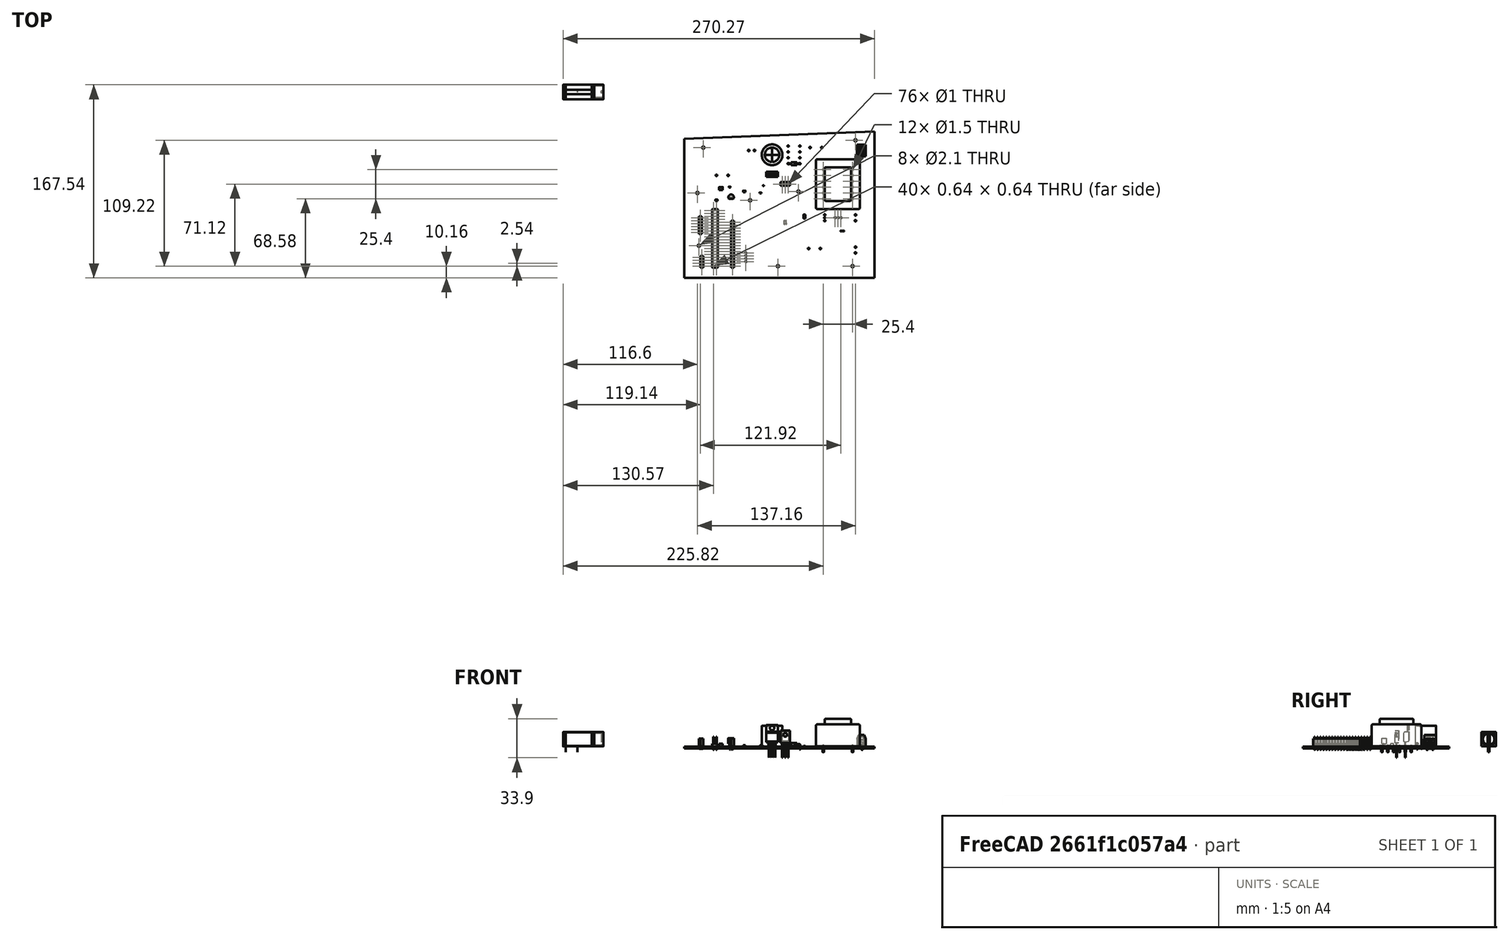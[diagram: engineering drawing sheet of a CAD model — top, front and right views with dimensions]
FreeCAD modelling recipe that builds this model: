
FCSTD DOCUMENT  (FreeCAD 0.19R24267 (Git))
Label: pcb_cad
License: All rights reserved
LicenseURL: http://en.wikipedia.org/wiki/All_rights_reserved
objects: App::Link×29, Part::Feature×23, App::Part×5, PartDesign::CoordinateSystem×1, Sketcher::SketchObject×1, Part::Compound2×1
note: 25 computed .brp shape members not serialized (recipe doc carries the construction recipe); baked Part::Feature solids carry a one-line shape summary decoded from their .brp

FEATURE [PartDesign::CoordinateSystem] Local_CS_53f5
  AttacherType = Attacher::AttachEngine3D
FEATURE [Part::Feature] Pcb_53f5
  shape: bbox 165.1 x 127 x 1.6 mm, 138 faces (baked)
FEATURE [Sketcher::SketchObject] PCB_Sketch_53f5
  FullyConstrained = false
  sketch-geometry (4):
    g0: LineSegment StartX=267.97 StartY=-34.29 StartZ=0 EndX=102.87 EndY=-40.64 EndZ=0
    g1: LineSegment StartX=267.97 StartY=-161.29 StartZ=0 EndX=267.97 EndY=-34.29 EndZ=0
    g2: LineSegment StartX=102.87 StartY=-161.29 StartZ=0 EndX=267.97 EndY=-161.29 EndZ=0
    g3: LineSegment StartX=102.87 StartY=-40.64 StartZ=0 EndX=102.87 EndY=-161.29 EndZ=0
  constraints (4):
    c: Coincident(g2,g3)
    c: Coincident(g0,g3)
    c: Coincident(g1,g2)
    c: Coincident(g0,g1)
FEATURE [App::Part] Board_Geoms_53f5
  Group = -> [Local_CS_53f5,Pcb_53f5,PCB_Sketch_53f5]
  Origin = -> Origin
FEATURE [Part::Feature] Shape  label="P1_User Library-Terminal-Screw-3A-2way_606F4117"
  Placement = pos=(256.54,-50.8,0) rot=(0.57735,0.57735,0.57735;2.0944rad)
  shape: bbox 7.6 x 10.6 x 13 mm, 121 faces (baked)
FEATURE [App::Link] P1_User_Library_Terminal_Screw_3A_2way_606F4117_ln_  label="J8_User Library-Terminal-Screw-3A-2way_606F4101"
  LinkPlacement = pos=(251.46,-137.16,0) rot=(0.57735,0.57735,0.57735;2.0944rad)
  LinkedObject = -> Shape
  Placement = pos=(251.46,-137.16,0) rot=(0.57735,0.57735,0.57735;2.0944rad)
FEATURE [App::Link] P1_User_Library_Terminal_Screw_3A_2way_606F4117_ln_001  label="J2_User Library-Terminal-Screw-3A-2way_606DFC80"
  LinkPlacement = pos=(161.29,-50.8,0) rot=(0,0.707107,0.707107;3.14159rad)
  LinkedObject = -> Shape
  Placement = pos=(161.29,-50.8,0) rot=(0,0.707107,0.707107;3.14159rad)
FEATURE [Part::Feature] Shape001  label="J1_PinHeader_2x20_P254mm_Vertical_606DFC5E"
  Placement = pos=(128.27,-102.87,0) rot=(0,0,1;0rad)
  shape: bbox 5.08 x 50.8 x 11.54 mm, 844 faces (baked)
FEATURE [Part::Feature] Shape002  label="R1_R_1206_3216Metric_606F4180"
  Placement = pos=(207.01,-108.142,0) rot=(0,0,-1;1.5708rad)
  shape: bbox 1.6 x 3.2 x 0.55 mm, 26 faces (baked)
FEATURE [Part::Feature] Shape003  label="D11_D_1206_606F3DCA"
  Placement = pos=(190.5,-113.16,-1.6) rot=(0.707107,0.707107,0;3.14159rad)
  shape: bbox 1.87 x 3.4 x 0.96 mm, 39 faces (baked)
FEATURE [Part::Feature] Shape004  label="U2_TO-220-3_Vertical_606F427F"
  Placement = pos=(176.53,-72.39,0) rot=(0,0,1;0rad)
  shape: bbox 10.25 x 4.455 x 28.53 mm, 48 faces (baked)
FEATURE [App::Link] U2_TO_220_3_Vertical_606F427F_ln_  label="U1_TO-220-3_Vertical_606F4265"
  LinkPlacement = pos=(224.79,-106.68,0) rot=(0,0,-1;1.5708rad)
  LinkedObject = -> Shape004
  Placement = pos=(224.79,-106.68,0) rot=(0,0,-1;1.5708rad)
FEATURE [Part::Feature] Shape005  label="T1_Transformer_37x046_606F424B"
  Placement = pos=(248.92,-72.39,0) rot=(0,0,-1;1.5708rad)
  shape: bbox 38.1 x 43.18 x 29.15 mm, 83 faces, 13 solids (baked)
FEATURE [App::Link] R1_R_1206_3216Metric_606F4180_ln_  label="R11_R_1206_3216Metric_606F422A"
  LinkPlacement = pos=(151.13,-82.55,0) rot=(0,0,1;0rad)
  LinkedObject = -> Shape002
  Placement = pos=(151.13,-82.55,0) rot=(0,0,1;0rad)
FEATURE [App::Link] R1_R_1206_3216Metric_606F4180_ln_001  label="R10_R_1206_3216Metric_606F4219"
  LinkPlacement = pos=(190.5,-106.873,-1.6) rot=(0.707107,0.707107,0;3.14159rad)
  LinkedObject = -> Shape002
  Placement = pos=(190.5,-106.873,-1.6) rot=(0.707107,0.707107,0;3.14159rad)
FEATURE [App::Link] R1_R_1206_3216Metric_606F4180_ln_002  label="R9_R_1206_3216Metric_606F4208"
  LinkPlacement = pos=(187.96,-66.04,0) rot=(0,0,1;3.14159rad)
  LinkedObject = -> Shape002
  Placement = pos=(187.96,-66.04,0) rot=(0,0,1;3.14159rad)
FEATURE [App::Link] R1_R_1206_3216Metric_606F4180_ln_003  label="R8_R_1206_3216Metric_606F41F7"
  LinkPlacement = pos=(177.8,-83.82,0) rot=(0,0,1;0rad)
  LinkedObject = -> Shape002
  Placement = pos=(177.8,-83.82,0) rot=(0,0,1;0rad)
FEATURE [App::Link] R1_R_1206_3216Metric_606F4180_ln_004  label="R7_R_1206_3216Metric_606F41E6"
  LinkPlacement = pos=(216.94,-105.984,-1.6) rot=(-0.707107,0.707107,0;3.14159rad)
  LinkedObject = -> Shape002
  Placement = pos=(216.94,-105.984,-1.6) rot=(-0.707107,0.707107,0;3.14159rad)
FEATURE [Part::Feature] Shape006  label="R6_R_0402_1005Metric_606F41D5"
  Placement = pos=(171.45,-81.28,0) rot=(0,0,1;3.14159rad)
  shape: bbox 1 x 0.5 x 0.35 mm, 26 faces (baked)
FEATURE [App::Link] R6_R_0402_1005Metric_606F41D5_ln_  label="R5_R_0402_1005Metric_606F41C4"
  LinkPlacement = pos=(212.09,-118.87,0) rot=(0,0,-1;1.5708rad)
  LinkedObject = -> Shape006
  Placement = pos=(212.09,-118.87,0) rot=(0,0,-1;1.5708rad)
FEATURE [App::Link] R1_R_1206_3216Metric_606F4180_ln_005  label="R4_R_1206_3216Metric_606F41B3"
  LinkPlacement = pos=(168.91,-77.47,0) rot=(0,0,1;3.14159rad)
  LinkedObject = -> Shape002
  Placement = pos=(168.91,-77.47,0) rot=(0,0,1;3.14159rad)
FEATURE [App::Link] R1_R_1206_3216Metric_606F4180_ln_006  label="R3_R_1206_3216Metric_606F41A2"
  LinkPlacement = pos=(216.94,-111.594,0) rot=(0,0,1;1.5708rad)
  LinkedObject = -> Shape002
  Placement = pos=(216.94,-111.594,0) rot=(0,0,1;1.5708rad)
FEATURE [App::Link] R1_R_1206_3216Metric_606F4180_ln_007  label="R2_R_1206_3216Metric_606F4191"
  LinkPlacement = pos=(168.91,-72.39,0) rot=(0,0,1;0rad)
  LinkedObject = -> Shape002
  Placement = pos=(168.91,-72.39,0) rot=(0,0,1;0rad)
FEATURE [Part::Feature] Shape007  label="Q4_TO-92_Inline_Narrow_606F416F"
  Placement = pos=(142.24,-91.44,0) rot=(0,0,1;0rad)
  shape: bbox 4.83 x 3.745 x 9.8 mm, 19 faces (baked)
FEATURE [App::Link] Q4_TO_92_Inline_Narrow_606F416F_ln_  label="Q3_TO-92_Inline_Narrow_606F415D"
  LinkPlacement = pos=(238.76,-120.65,0) rot=(0,0,1;0rad)
  LinkedObject = -> Shape007
  Placement = pos=(238.76,-120.65,0) rot=(0,0,1;0rad)
FEATURE [Part::Feature] Shape008  label="Q2_TO-126-3_Vertical_606F414B"
  Placement = pos=(187.96,-80.01,0) rot=(0,0,1;0rad)
  shape: bbox 8 x 3.25 x 23.75 mm, 66 faces (baked)
FEATURE [App::Link] Q2_TO_126_3_Vertical_606F414B_ln_  label="Q1_TO-126-3_Vertical_606F4131"
  LinkPlacement = pos=(233.68,-109.22,0) rot=(0,0,1;0rad)
  LinkedObject = -> Shape008
  Placement = pos=(233.68,-109.22,0) rot=(0,0,1;0rad)
FEATURE [Part::Feature] Shape009  label="J7_PinSocket_1x04_P254mm_Vertical_606F40ED"
  Placement = pos=(118.11,-143.51,0) rot=(0,0,1;0rad)
  shape: bbox 2.54 x 10.16 x 10.1 mm, 134 faces (baked)
FEATURE [App::Link] P1_User_Library_Terminal_Screw_3A_2way_606F4117_ln_002  label="J4_User Library-Terminal-Screw-3A-2way_606F4061"
  LinkPlacement = pos=(251.46,-109.22,0) rot=(0.57735,0.57735,0.57735;2.0944rad)
  LinkedObject = -> Shape
  Placement = pos=(251.46,-109.22,0) rot=(0.57735,0.57735,0.57735;2.0944rad)
FEATURE [Part::Feature] Solid
  shape: bbox 35.1 x 13.53 x 13.53 mm, 68 faces (baked)
FEATURE [Part::Feature] Solid001
  shape: bbox 0.2 x 1 x 5 mm, 8 faces (baked)
FEATURE [Part::Feature] Solid002
  shape: bbox 0.2 x 1 x 5 mm, 8 faces (baked)
FEATURE [Part::Compound2] Compound  label="F3_A_Bulgin_FX0457_606F64BC"
  Links = -> [Solid,Solid001,Solid002]
  Placement = pos=(130.81,-72.39,0) rot=(0,0,1;0rad)
FEATURE [App::Link] F3_A_Bulgin_FX0457_606F64BC_ln_  label="F2_A_Bulgin_FX0457_606F3E39"
  LinkPlacement = pos=(210.82,-135.89,0) rot=(0,0,1;0rad)
  LinkedObject = -> Compound
  Placement = pos=(210.82,-135.89,0) rot=(0,0,1;0rad)
FEATURE [App::Link] F3_A_Bulgin_FX0457_606F64BC_ln_001  label="F1_A_Bulgin_FX0457_606F3E1E"
  LinkPlacement = pos=(212.09,-48.26,0) rot=(0,0,1;0rad)
  LinkedObject = -> Compound
  Placement = pos=(212.09,-48.26,0) rot=(0,0,1;0rad)
FEATURE [Part::Feature] Shape010  label="D14_D_0805_606F3E03"
  Placement = pos=(130.81,-93.98,0) rot=(0,0,1;0rad)
  shape: bbox 2 x 1.27 x 0.8 mm, 39 faces (baked)
FEATURE [Part::Feature] Shape011  label="D13_D_0603_606F3DF0"
  Placement = pos=(142.24,-82.55,0) rot=(0,0,1;0rad)
  shape: bbox 1.6 x 0.87 x 0.66 mm, 39 faces (baked)
FEATURE [App::Link] D14_D_0805_606F3E03_ln_  label="D12_D_0805_606F3DDD"
  LinkPlacement = pos=(234.95,-116.84,0) rot=(0,0,1;0rad)
  LinkedObject = -> Shape010
  Placement = pos=(234.95,-116.84,0) rot=(0,0,1;0rad)
FEATURE [App::Link] D13_D_0603_606F3DF0_ln_  label="D10_D_0603_606F62C1"
  LinkPlacement = pos=(168.91,-83.82,0) rot=(0,0,1;0rad)
  LinkedObject = -> Shape011
  Placement = pos=(168.91,-83.82,0) rot=(0,0,1;0rad)
FEATURE [App::Link] D11_D_1206_606F3DCA_ln_  label="D9_D_1206_606F3DA4"
  LinkPlacement = pos=(210.82,-106.55,-1.6) rot=(0.707107,0.707107,0;3.14159rad)
  LinkedObject = -> Shape003
  Placement = pos=(210.82,-106.55,-1.6) rot=(0.707107,0.707107,0;3.14159rad)
FEATURE [App::Part] Bot_53f5
  Group = -> [Shape003,R1_R_1206_3216Metric_606F4180_ln_001,R1_R_1206_3216Metric_606F4180_ln_004,D11_D_1206_606F3DCA_ln_]
  Origin = -> Origin004
FEATURE [Part::Feature] Shape012  label="D8_LED_0603_1608Metric_606F3D91"
  Placement = pos=(168.91,-87.63,0) rot=(0,0,1;0rad)
  shape: bbox 1.6 x 0.8 x 1.1 mm, 50 faces (baked)
FEATURE [App::Link] D8_LED_0603_1608Metric_606F3D91_ln_  label="D7_LED_0603_1608Metric_606F3D7E"
  LinkPlacement = pos=(213.36,-124.46,0) rot=(0,0,1;0rad)
  LinkedObject = -> Shape012
  Placement = pos=(213.36,-124.46,0) rot=(0,0,1;0rad)
FEATURE [Part::Feature] Shape013  label="D6_D_DO-41_SOD81_P10.16mm_Horizontal_606F49EC"
  Placement = pos=(203.2,-62.23,0) rot=(0,0,1;3.14159rad)
  shape: bbox 11.16 x 2.72 x 5.71 mm, 15 faces (baked)
FEATURE [App::Link] D6_D_DO_41_SOD81_P10_16mm_Horizontal_606F49EC_ln_  label="D5_D_DO-41_SOD81_P10.16mm_Horizontal_606F3D4C"
  LinkPlacement = pos=(193.04,-57.15,0) rot=(0,0,1;0rad)
  LinkedObject = -> Shape013
  Placement = pos=(193.04,-57.15,0) rot=(0,0,1;0rad)
FEATURE [App::Link] D8_LED_0603_1608Metric_606F3D91_ln_001  label="D4_LED_0603_1608Metric_606F3D2D"
  LinkPlacement = pos=(179.07,-90.17,0) rot=(0,0,1;0rad)
  LinkedObject = -> Shape012
  Placement = pos=(179.07,-90.17,0) rot=(0,0,1;0rad)
FEATURE [App::Link] D8_LED_0603_1608Metric_606F3D91_ln_002  label="D3_LED_0603_1608Metric_606F3D1A"
  LinkPlacement = pos=(246.863,-125.73,0) rot=(0,0,1;0rad)
  LinkedObject = -> Shape012
  Placement = pos=(246.863,-125.73,0) rot=(0,0,1;0rad)
FEATURE [App::Link] D6_D_DO_41_SOD81_P10_16mm_Horizontal_606F49EC_ln_001  label="D2_D_DO-41_SOD81_P10.16mm_Horizontal_606F3D07"
  LinkPlacement = pos=(193.04,-52.07,0) rot=(0,0,1;0rad)
  LinkedObject = -> Shape013
  Placement = pos=(193.04,-52.07,0) rot=(0,0,1;0rad)
FEATURE [App::Link] D6_D_DO_41_SOD81_P10_16mm_Horizontal_606F49EC_ln_002  label="D1_D_DO-41_SOD81_P10.16mm_Horizontal_606F3CE8"
  LinkPlacement = pos=(193.04,-46.99,0) rot=(0,0,1;0rad)
  LinkedObject = -> Shape013
  Placement = pos=(193.04,-46.99,0) rot=(0,0,1;0rad)
FEATURE [Part::Feature] Shape014  label="C5_C_0805_2012Metric_606F3CC9"
  Placement = pos=(154.94,-86.36,0) rot=(0,0,1;0rad)
  shape: bbox 2 x 1.25 x 1.25 mm, 28 faces (baked)
FEATURE [Part::Feature] Shape015  label="C4_C_1210_3225Metric_606F3CB8"
  Placement = pos=(134.62,-83.82,0) rot=(0,0,1;3.14159rad)
  shape: bbox 3.2 x 2.5 x 2.5 mm, 28 faces (baked)
FEATURE [App::Link] C5_C_0805_2012Metric_606F3CC9_ln_  label="C3_C_0805_2012Metric_606F3CA7"
  LinkPlacement = pos=(249.24,-118.11,0) rot=(0,0,1;0rad)
  LinkedObject = -> Shape014
  Placement = pos=(249.24,-118.11,0) rot=(0,0,1;0rad)
FEATURE [App::Link] C4_C_1210_3225Metric_606F3CB8_ln_  label="C2_C_1210_3225Metric_606F3C96"
  LinkPlacement = pos=(228.395,-121.92,0) rot=(0,0,1;0rad)
  LinkedObject = -> Shape015
  Placement = pos=(228.395,-121.92,0) rot=(0,0,1;0rad)
FEATURE [Part::Feature] Shape016  label="C1_CP_Radial_D180mm_P750mm_606F3C85"
  Placement = pos=(179.07,-50.8,0) rot=(0,0,-1;1.5708rad)
  shape: bbox 23.01 x 22.24 x 20 mm, 50 faces (baked)
FEATURE [App::Link] J7_PinSocket_1x04_P254mm_Vertical_606F40ED_ln_  label="J6_PinSocket_1x04_P254mm_Vertical_606DFF17"
  LinkPlacement = pos=(156.21,-139.7,0) rot=(0,0,1;0rad)
  LinkedObject = -> Shape009
  Placement = pos=(156.21,-139.7,0) rot=(0,0,1;0rad)
FEATURE [Part::Feature] Shape017  label="J5_PinSocket_1x16_P254mm_Vertical_606DFCD8"
  Placement = pos=(144.78,-113.03,0) rot=(0,0,1;0rad)
  shape: bbox 2.54 x 40.64 x 10.1 mm, 506 faces (baked)
FEATURE [Part::Feature] Shape018  label="J3_PinSocket_1x06_P254mm_Vertical_606DFC9A"
  Placement = pos=(116.84,-121.92,0) rot=(0,0,1;3.14159rad)
  shape: bbox 2.54 x 15.24 x 10.1 mm, 196 faces (baked)
FEATURE [App::Part] Top_53f5
  Group = -> [Shape,P1_User_Library_Terminal_Screw_3A_2way_606F4117_ln_,P1_User_Library_Terminal_Screw_3A_2way_606F4117_ln_001,Shape001,Shape002,Shape004,U2_TO_220_3_Vertical_606F427F_ln_,Shape005,R1_R_1206_3216Metric_606F4180_ln_,R1_R_1206_3216Metric_606F4180_ln_002,R1_R_1206_3216Metric_606F4180_ln_003,Shape006,R6_R_0402_1005Metric_606F41D5_ln_,R1_R_1206_3216Metric_606F4180_ln_005,+34 more]
  Origin = -> Origin003
FEATURE [App::Part] Step_Models_53f5
  Group = -> [Top_53f5,Bot_53f5]
  Origin = -> Origin002
FEATURE [App::Part] Board_53f5  label="protection"
  Group = -> [Board_Geoms_53f5,Step_Models_53f5]
  Origin = -> Origin001
